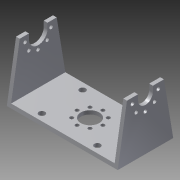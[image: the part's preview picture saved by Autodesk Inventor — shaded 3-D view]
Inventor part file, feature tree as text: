
AUTODESK INVENTOR PART (.ipt)
format: ipt  version: 2013 (Build 170138000, 138)  size: 198,656 bytes
history: native  units: mm
features: sketch x8, extrude x4, hole x4, pattern_circular x2, other x1
ambient origin geometry x8: Origin, YZ Plane, XZ Plane, XY Plane, X Axis, Y Axis, Z Axis, Center Point
feature tree (19):
  other  "ソリッド1"
  extrude  "押し出し1"  Depth=60.0mm
  extrude  "押し出し2"  Depth=30.0mm
  extrude  "押し出し3"  Depth=28.0mm
  extrude  "押し出し4"  Depth=56.0mm
  hole  "穴2"  [1 undecoded]
  hole  "穴3"  [1 undecoded]
  pattern_circular  "円形状パターン2"  Count=3  [1 undecoded]
  hole  "穴4"  [1 undecoded]
  pattern_circular  "円形状パターン3"  [2 undecoded]
  hole  "穴5"  [1 undecoded]
  sketch  "スケッチ1"
  sketch  "スケッチ2"
  sketch  "スケッチ3"
  sketch  "スケッチ4"
  sketch  "スケッチ7"
  sketch  "スケッチ8"
  sketch  "スケッチ9"
  sketch  "スケッチ10"
note: 7 required parameter values undecoded (feature->parameter linkage not recoverable at this tier; creation-order binding heuristic only, values carry confidence <= 0.55)
